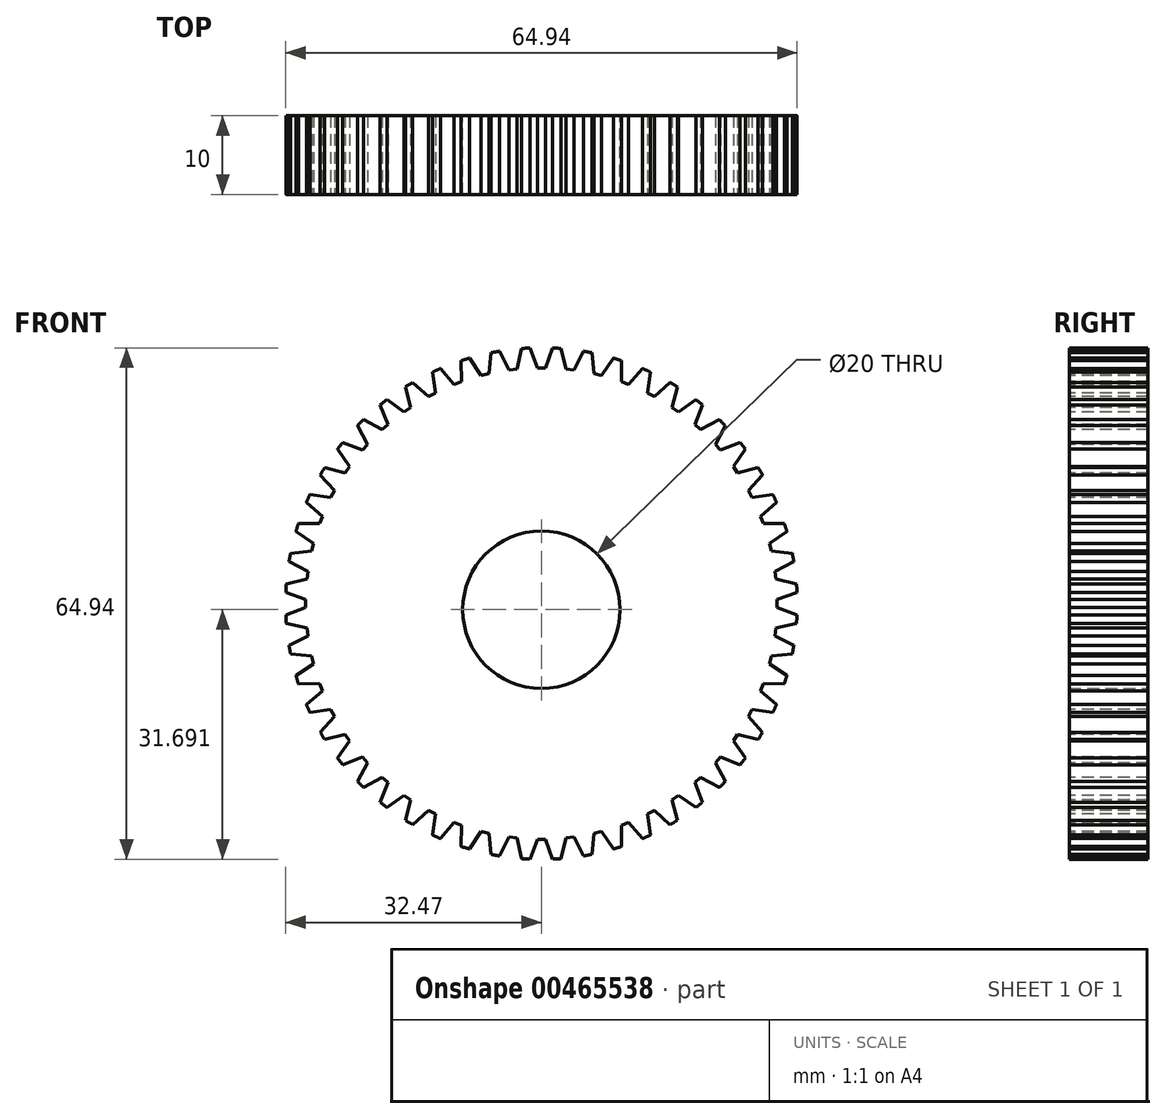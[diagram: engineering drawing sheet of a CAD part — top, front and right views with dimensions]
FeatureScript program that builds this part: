
annotation { "Feature Type Name" : "Feature", "Feature Type Description" : "" }
export const myFeature = defineFeature(function(context is Context, id is Id, definition is map)
    precondition{}
    {
        {
            var Q0;
            Q0=qCreatedBy(makeId("Front.planeOp"),FACE);
            var sketch = newSketch(context, id + "F0", { "sketchPlane" : qUnion([Q0])});
            skCircle(sketch, "E0", {"center": v(0, -0.78) * mm, "radius": 10 * mm});
            skCircle(sketch, "E1", {"center": v(0, 0) * mm, "radius": 32.5 * mm});
            skSolve(sketch);
        }
        {
            var Q0;
            Q0=makeQuery(id+"F0.imprint","IMPRINT",FACE,{"disambiguationData":[TD([[makeQuery(id+"F0.imprint","IMPRINT",EDGE,{"derivedFrom":sQuery(id+"F0.wireOp",EDGE,"E0")}),-1.0]])]});
            extrude(context, id + "F1", {"entities" : qUnion([Q0]), "depth" : 10 * mm});
        }
        {
            var Q0;
            Q0=makeQuery(id+"F1.opExtrude","CAP_FACE",FACE,{"disambiguationData":[OSD([sQuery(id+"F0.wireOp",EDGE,"E0"),sQuery(id+"F0.wireOp",EDGE,"E1")])],"isStart":false});
            var sketch = newSketch(context, id + "F2", { "sketchPlane" : qUnion([Q0])});
            skLineSegment(sketch, "E2", {"start": v(0, 0) * mm, "end": v(0, 32.5) * mm, "construction": true});
            skLineSegment(sketch, "E3", {"start": v(0, 29.95) * mm, "end": v(0, 32.5) * mm});
            skLineSegment(sketch, "E4", {"start": v(0, 29.95) * mm, "end": v(0.5, 29.95) * mm});
            skLineSegment(sketch, "E5", {"start": v(0, 29.95) * mm, "end": v(-0.5, 29.95) * mm});
            skLineSegment(sketch, "E6", {"start": v(-0.5, 29.95) * mm, "end": v(-1.42, 32.47) * mm});
            skLineSegment(sketch, "E7", {"start": v(0.5, 29.95) * mm, "end": v(1.42, 32.47) * mm});
            skSolve(sketch);
        }
        {
            var Q0;
            Q0 = qSketchRegion(id + "F2", true);
            var Q1;
            {var subQ0=sQuery(id+"F2.wireOp",EDGE,"E3");Q1=makeQuery(id+"F2.imprint","IMPRINT",FACE,{"disambiguationData":[TD([[makeQuery(id+"F2.imprint","IMPRINT",EDGE,{"derivedFrom":subQ0}),1.0]])]});}
            var Q2;
            {var subQ0=sQuery(id+"F2.wireOp",EDGE,"E3");Q2=makeQuery(id+"F2.imprint","IMPRINT",FACE,{"disambiguationData":[TD([[makeQuery(id+"F2.imprint","IMPRINT",EDGE,{"derivedFrom":subQ0}),-1.0]])]});}
            extrude(context, id + "F3", {"entities" : qUnion([Q0, Q1, Q2]), "operationType" : NewBodyOperationType.REMOVE, "oppositeDirection" : true, "depth" : 25 * mm});
        }
        {
            var Q0;
            Q0=makeQuery(id+"F3.boolean.opBoolean","COPY",FACE,{"derivedFrom":makeQuery(id+"F3.opExtrude","SWEPT_FACE",FACE,{"disambiguationData":[OSD([sQuery(id+"F2.wireOp",EDGE,"E6")])]})});
            var Q1;
            Q1=makeQuery(id+"F3.boolean.opBoolean","COPY",FACE,{"derivedFrom":makeQuery(id+"F3.opExtrude","SWEPT_FACE",FACE,{"disambiguationData":[OSD([sQuery(id+"F2.wireOp",EDGE,"E4"),sQuery(id+"F2.wireOp",EDGE,"E5")])]})});
            var Q2;
            Q2=makeQuery(id+"F3.boolean.opBoolean","COPY",FACE,{"derivedFrom":makeQuery(id+"F3.opExtrude","SWEPT_FACE",FACE,{"disambiguationData":[OSD([sQuery(id+"F2.wireOp",EDGE,"E7")])]})});
            var Q3;
            Q3=makeQuery(id+"F1.opExtrude","SWEPT_FACE",FACE,{"disambiguationData":[OSD([sQuery(id+"F0.wireOp",EDGE,"E1")])]});
            circularPattern(context, id + "F4", {"patternType" : PatternType.FACE, "faces" : qUnion([Q0, Q1, Q2]), "axis" : qUnion([Q3]), "angle" : 360 * degree, "instanceCount" : 52, "equalSpace" : true});
        }
    });
